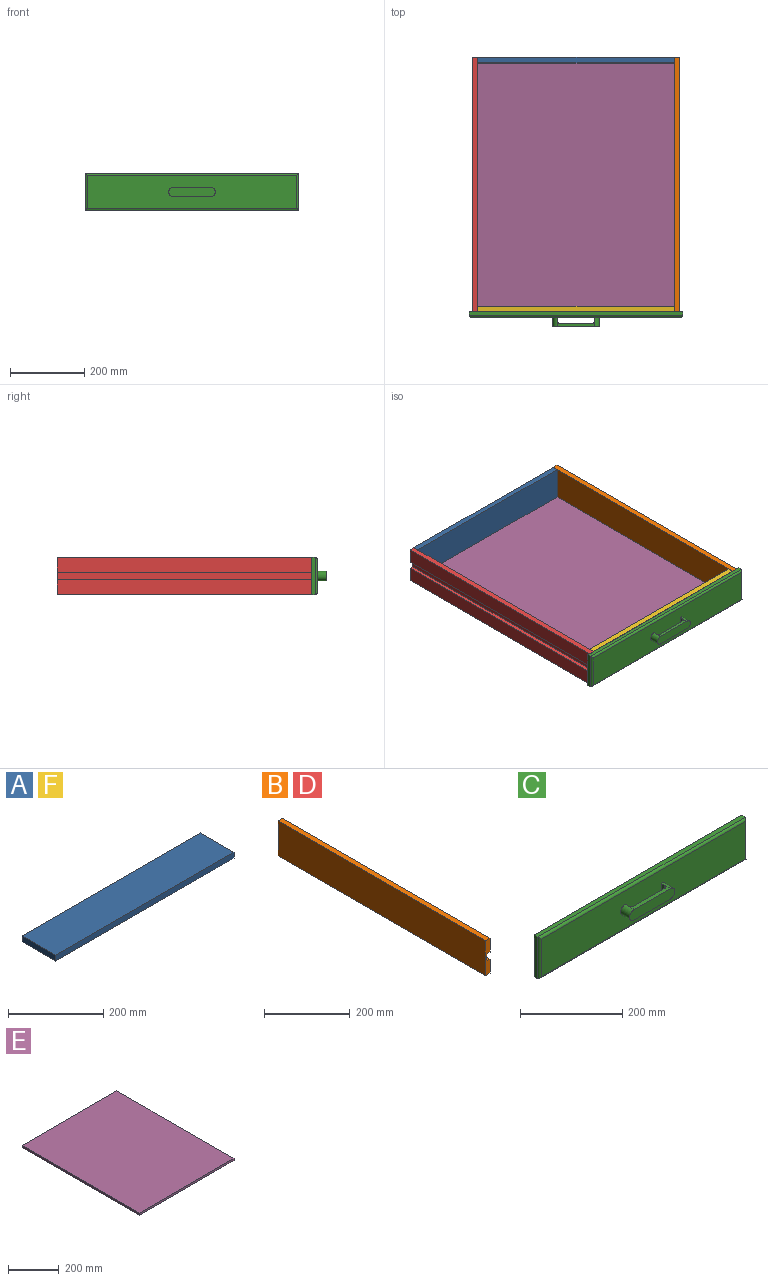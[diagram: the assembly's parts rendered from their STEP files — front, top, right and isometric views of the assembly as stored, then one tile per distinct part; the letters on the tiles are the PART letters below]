
ASSEMBLY  parts=6 mates=5
PART A: 6 faces, bbox 530x100x15 mm
  f0: plane 100x15mm, normal (1,0,0), area 1500mm2, adj f1,f3,f4,f5
  f1: plane 530x15mm, normal (0,1,0), area 7950mm2, adj f0,f2,f4,f5
  f2: plane 100x15mm, normal (-1,0,0), area 1500mm2, adj f1,f3,f4,f5
  f3: plane 530x15mm, normal (0,-1,0), area 7950mm2, adj f0,f2,f4,f5
  f4: plane 530x100mm, normal (0,0,1), area 53000mm2, adj f0,f1,f2,f3
  f5: plane 530x100mm, normal (0,0,-1), area 53000mm2, adj f0,f1,f2,f3
PART B: 10 faces, bbox 15x684.9x100 mm
  f0: plane 684.9x40mm, normal (1,0,0), area 27396mm2, adj f1,f2,f3,f7
  f1: plane 100x15mm, normal (0,1,0), area 1300mm2, adj f0,f2,f4,f5,f6,f7,f8,f9
  f2: plane 684.9x15mm, normal (0,0,1), area 10273.5mm2, adj f0,f1,f3,f6
  f3: plane 100x15mm, normal (0,-1,0), area 1300mm2, adj f0,f2,f4,f5,f6,f7,f8,f9
  f4: plane 684.9x15mm, normal (0,0,-1), area 10273.5mm2, adj f1,f3,f5,f6
  f5: plane 684.9x40mm, normal (1,0,0), area 27396mm2, adj f1,f3,f4,f8
  f6: plane 684.9x100mm, normal (-1,0,0), area 68490mm2, adj f1,f2,f3,f4
  f7: plane 684.9x10mm, normal (0,0,-1), area 6849mm2, adj f0,f1,f3,f9
  f8: plane 684.9x10mm, normal (0,0,1), area 6849mm2, adj f1,f3,f5,f9
  f9: plane 684.9x20mm, normal (1,0,0), area 13698mm2, adj f1,f3,f7,f8
PART C: 20 faces, bbox 575x40x100 mm
  f0: plane 100x10mm, normal (1,0,0), area 1000mm2, adj f1,f3,f5,f6
  f1: plane 575x10mm, normal (0,0,1), area 5750mm2, adj f0,f2,f5,f7
  f2: plane 100x10mm, normal (-1,0,0), area 1000mm2, adj f1,f3,f5,f9
  f3: plane 575x10mm, normal (0,0,-1), area 5750mm2, adj f0,f2,f5,f8
  f4: plane 565x90mm, normal (0,-1,0), area 50359.1mm2, adj f6,f7,f8,f9,f11,f13,f15,f19
  f5: plane 575x100mm, normal (0,1,0), area 57500mm2, adj f0,f1,f2,f3
  f6: cylinder r=5mm len=100mm, axis (0,0,-1), area 756.9mm2, adj f0,f4,f7,f8
  f7: cylinder r=5mm len=575mm, axis (1,0,0), area 4487.5mm2, adj f1,f4,f6,f9
  f8: cylinder r=5mm len=575mm, axis (-1,0,0), area 4487.5mm2, adj f3,f4,f6,f9
  f9: cylinder r=5mm len=100mm, axis (0,0,1), area 756.9mm2, adj f2,f4,f7,f8
  f10: plane 100x15.47mm, normal (0,0,1), area 868.1mm2, adj f11,f13,f14,f16,f17,f18
  f11: cylinder r=12.5mm len=25mm, axis (0,1,0), area 981.7mm2, adj f4,f10,f12,f14,f15
  f12: plane 100x15.47mm, normal (0,0,-1), area 868.1mm2, adj f11,f13,f14,f16,f17,f18
  f13: cylinder r=12.5mm len=25mm, axis (0,1,0), area 981.7mm2, adj f4,f10,f12,f14,f19
  f14: plane 125x25mm, normal (0,-1,0), area 2990.9mm2, adj f10,f11,f12,f13
  f15: plane 25x9.53mm, normal (1,0,0), area 238.2mm2, adj f4,f11,f16
  f16: cylinder r=7mm len=25mm, axis (0,0,1), area 274.9mm2, adj f10,f12,f15,f17
  f17: plane 86x25mm, normal (0,1,0), area 2150mm2, adj f10,f12,f16,f18
  f18: cylinder r=7mm len=25mm, axis (0,0,1), area 274.9mm2, adj f10,f12,f17,f19
  f19: plane 25x9.53mm, normal (-1,0,0), area 238.2mm2, adj f4,f13,f18
PART D: same geometry as B
PART E: 6 faces, bbox 530x654.9x10 mm
  f0: plane 654.9x10mm, normal (1,0,0), area 6549mm2, adj f1,f3,f4,f5
  f1: plane 530x10mm, normal (0,1,0), area 5300mm2, adj f0,f2,f4,f5
  f2: plane 654.9x10mm, normal (-1,0,0), area 6549mm2, adj f1,f3,f4,f5
  f3: plane 530x10mm, normal (0,-1,0), area 5300mm2, adj f0,f2,f4,f5
  f4: plane 654.9x530mm, normal (0,0,1), area 347097mm2, adj f0,f1,f2,f3
  f5: plane 654.9x530mm, normal (0,0,-1), area 347097mm2, adj f0,f1,f2,f3
PART F: same geometry as A
PLACE A rot(axis=(-1,0,0),90deg) t=(-280.45,893.92,71.89)mm
PLACE B rot(axis=(1,0,0),0deg) t=(-7.95,566.47,71.89)mm
PLACE C t=(-280.45,224.02,71.89)mm
PLACE D rot(axis=(0,0,-1),180deg) t=(-552.95,566.47,71.89)mm
PLACE E rot(axis=(1,0,0),0deg) t=(-288.58,566.47,21.89)mm
PLACE F rot(axis=(1,0,0),90deg) t=(-280.45,239.02,71.89)mm
MATE fastened D.f6 <-> A.f2  axis (1,0,0) through (-545.45,908.92,121.89)mm
MATE fastened B.f6 <-> A.f0  axis (-1,0,0) through (-15.45,908.92,121.89)mm
MATE fastened E.f1 <-> A.f5  axis (0,1,0) through (-545.45,893.92,21.89)mm
MATE fastened B.f6 <-> F.f0  axis (-1,0,0) through (-15.45,224.02,121.89)mm
MATE fastened C.f5 <-> F.f4  axis (0,1,0) through (-280.45,224.02,71.89)mm
